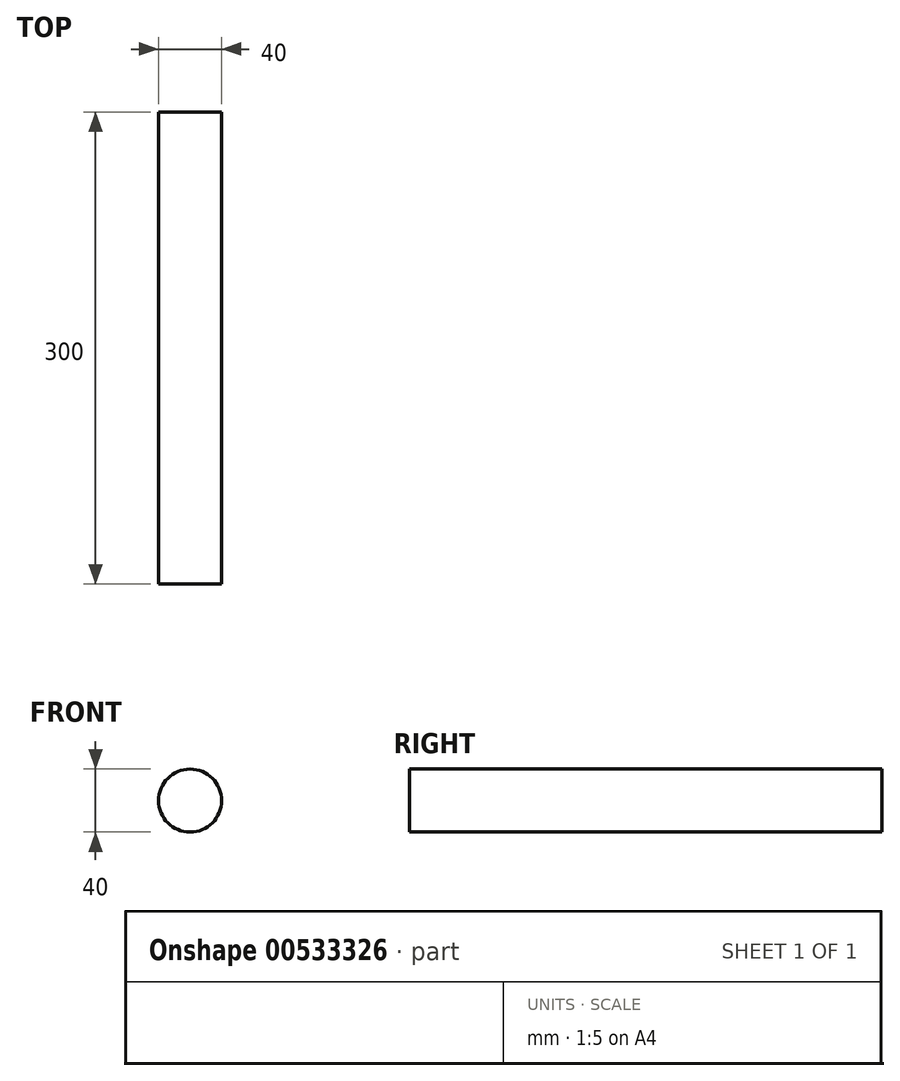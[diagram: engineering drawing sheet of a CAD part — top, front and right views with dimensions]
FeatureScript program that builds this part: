
annotation { "Feature Type Name" : "Feature", "Feature Type Description" : "" }
export const myFeature = defineFeature(function(context is Context, id is Id, definition is map)
    precondition{}
    {
        {
            var Q0;
            Q0=qCreatedBy(makeId("Front.planeOp"),FACE);
            var sketch = newSketch(context, id + "F0", { "sketchPlane" : qUnion([Q0])});
            skCircle(sketch, "E0", {"center": v(0, 0) * mm, "radius": 20 * mm});
            skSolve(sketch);
        }
        {
            var Q0;
            Q0=makeQuery(id+"F0.imprint","IMPRINT",FACE,{"disambiguationData":[TD([[makeQuery(id+"F0.imprint","IMPRINT",EDGE,{"derivedFrom":sQuery(id+"F0.wireOp",EDGE,"E0")}),1.0]])]});
            extrude(context, id + "F1", {"entities" : qUnion([Q0]), "depth" : 300 * mm, "offsetDistance" : 25 * mm});
        }
    });
